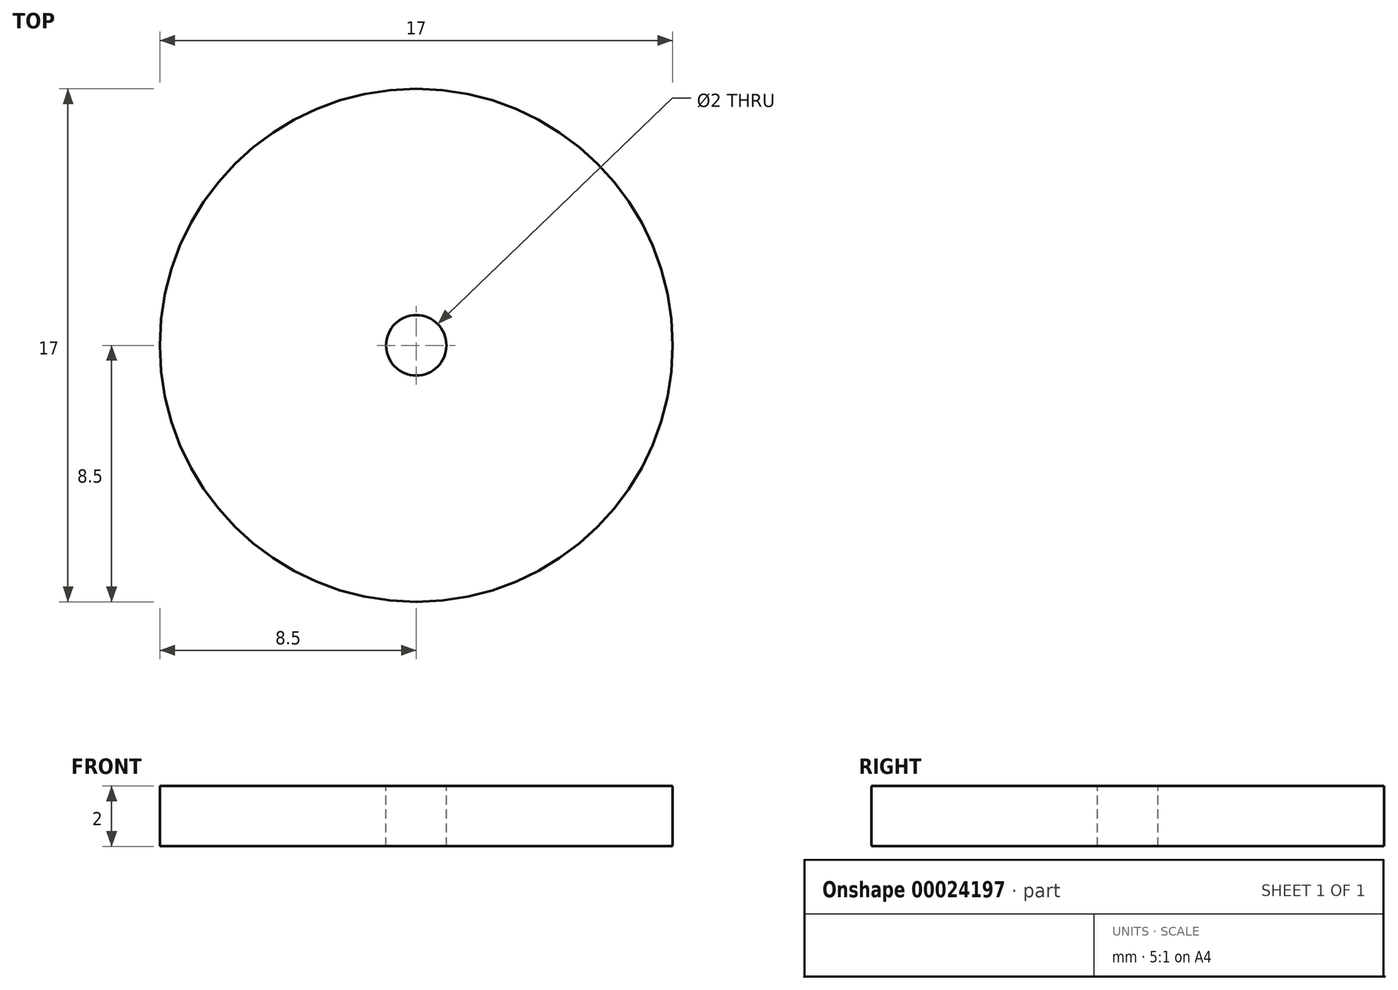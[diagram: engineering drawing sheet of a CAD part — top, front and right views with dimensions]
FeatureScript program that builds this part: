
annotation { "Feature Type Name" : "Feature", "Feature Type Description" : "" }
export const myFeature = defineFeature(function(context is Context, id is Id, definition is map)
    precondition{}
    {
        {
            var Q0;
            Q0=qCreatedBy(makeId("Front.planeOp"),FACE);
            var sketch = newSketch(context, id + "F0", { "sketchPlane" : qUnion([Q0])});
            skLineSegment(sketch, "E0", {"start": v(0, 25.96) * mm, "end": v(0, -28.58) * mm, "construction": true});
            skLineSegment(sketch, "E1.bottom", {"start": v(1, -14.16) * mm, "end": v(8.5, -14.16) * mm});
            skLineSegment(sketch, "E1.top", {"start": v(1, -16.16) * mm, "end": v(8.5, -16.16) * mm});
            skLineSegment(sketch, "E1.left", {"start": v(1, -14.16) * mm, "end": v(1, -16.16) * mm});
            skLineSegment(sketch, "E1.right", {"start": v(8.5, -14.16) * mm, "end": v(8.5, -16.16) * mm});
            skSolve(sketch);
        }
        {
            var Q0;
            Q0 = qSketchRegion(id + "F0", true);
            var Q1;
            Q1=sQuery(id+"F0.wireOp",EDGE,"E0");
            revolve(context, id + "F1", {"entities" : qUnion([Q0]), "axis" : qUnion([Q1]), "revolveType" : RevolveType.FULL});
        }
    });
